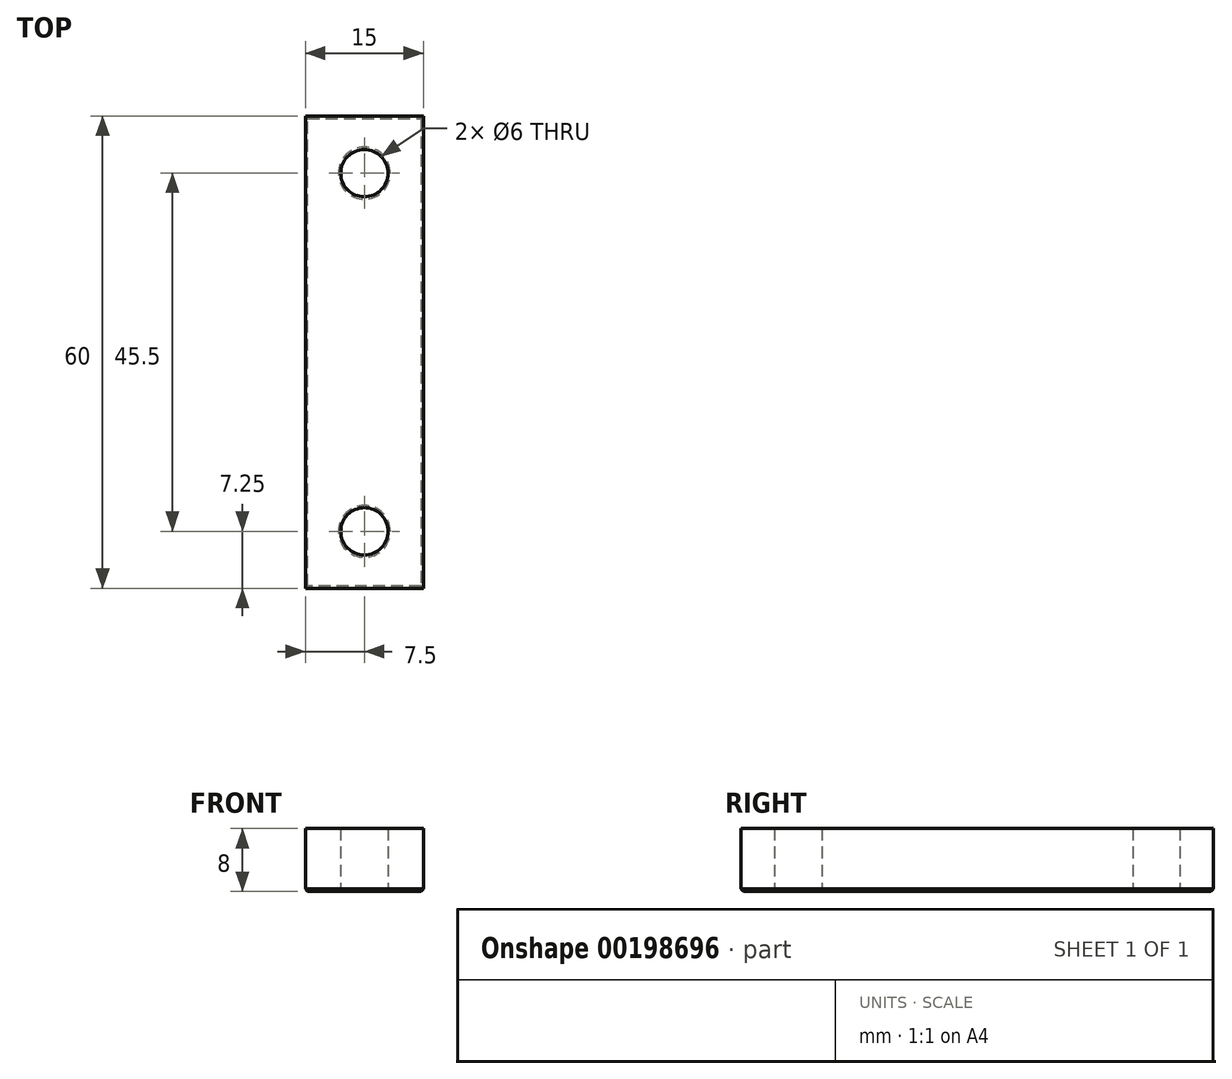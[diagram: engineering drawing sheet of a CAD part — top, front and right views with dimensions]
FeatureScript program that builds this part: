
annotation { "Feature Type Name" : "Feature", "Feature Type Description" : "" }
export const myFeature = defineFeature(function(context is Context, id is Id, definition is map)
    precondition{}
    {
        {
            var Q0;
            Q0=qCreatedBy(makeId("Top.planeOp"),FACE);
            var sketch = newSketch(context, id + "F0", { "sketchPlane" : qUnion([Q0])});
            skLineSegment(sketch, "E0.bottom", {"start": v(7.5, 30) * mm, "end": v(-7.5, 30) * mm});
            skLineSegment(sketch, "E0.top", {"start": v(7.5, -30) * mm, "end": v(-7.5, -30) * mm});
            skLineSegment(sketch, "E0.left", {"start": v(7.5, 30) * mm, "end": v(7.5, -30) * mm});
            skLineSegment(sketch, "E0.right", {"start": v(-7.5, 30) * mm, "end": v(-7.5, -30) * mm});
            skPoint(sketch, "E0.middle", {"position": v(0, 0) * mm});
            skCircle(sketch, "E1", {"center": v(0, 22.75) * mm, "radius": 3 * mm});
            skCircle(sketch, "E2.MirrorC", {"center": v(0, -22.75) * mm, "radius": 3 * mm});
            skSolve(sketch);
        }
        {
            var Q0;
            Q0 = qSketchRegion(id + "F0", true);
            extrude(context, id + "F1", {"entities" : qUnion([Q0]), "depth" : 8 * mm});
        }
        {
            var Q0;
            Q0=makeQuery(id+"F1.opExtrude","CAP_FACE",FACE,{"disambiguationData":[OSD([sQuery(id+"F0.wireOp",EDGE,"E0.bottom"),sQuery(id+"F0.wireOp",EDGE,"E0.top"),sQuery(id+"F0.wireOp",EDGE,"E0.left"),sQuery(id+"F0.wireOp",EDGE,"E0.right"),sQuery(id+"F0.wireOp",EDGE,"E1"),sQuery(id+"F0.wireOp",EDGE,"E2.MirrorC")])],"isStart":true});
            chamfer(context, id + "F2", {"entities" : qUnion([Q0]), "width" : 0.3 * mm});
        }
    });
